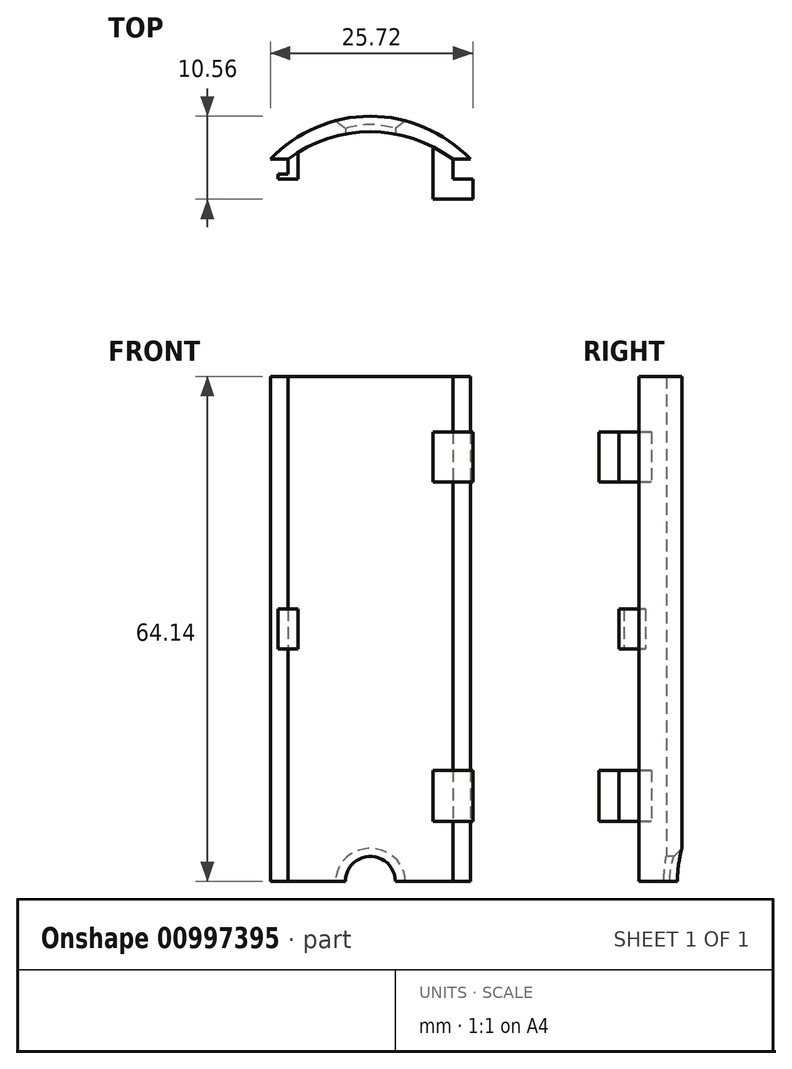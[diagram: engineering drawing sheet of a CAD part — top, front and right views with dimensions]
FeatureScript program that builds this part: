
annotation { "Feature Type Name" : "Feature", "Feature Type Description" : "" }
export const myFeature = defineFeature(function(context is Context, id is Id, definition is map)
    precondition{}
    {
        {
            var Q0;
            Q0=qCreatedBy(makeId("Top.planeOp"),FACE);
            var sketch = newSketch(context, id + "F0", { "sketchPlane" : qUnion([Q0])});
            skArc(sketch, "E0", {"start": v(-9.49, 0) * mm, "mid": v(-22.19, 5.48) * mm, "end": v(-34.89, 0) * mm});
            skPoint(sketch, "E1", {"position": v(-32.67, 0) * mm});
            skPoint(sketch, "E2", {"position": v(-11.7, 0) * mm});
            skArc(sketch, "E3", {"start": v(-11.7, 0) * mm, "mid": v(-22.19, 3.5) * mm, "end": v(-32.67, 0) * mm});
            skLineSegment(sketch, "E4", {"start": v(-34.89, 0) * mm, "end": v(-32.67, 0) * mm});
            skLineSegment(sketch, "E5", {"start": v(-11.7, 0) * mm, "end": v(-9.49, 0) * mm});
            skSolve(sketch);
        }
        {
            var Q0;
            Q0 = qSketchRegion(id + "F0", true);
            extrude(context, id + "F1", {"entities" : qUnion([Q0]), "depth" : 64.13 * mm, "offsetDistance" : 25.4 * mm});
        }
        {
            var Q0;
            Q0=qCreatedBy(makeId("Front.planeOp"),FACE);
            var sketch = newSketch(context, id + "F2", { "sketchPlane" : qUnion([Q0])});
            skLineSegment(sketch, "E6.0", {"start": v(-9.49, 0) * mm, "end": v(-34.89, 0) * mm});
            skCircle(sketch, "E7", {"center": v(-22.19, 0) * mm, "radius": 3.18 * mm});
            skSolve(sketch);
        }
        {
            var Q0;
            Q0 = qSketchRegion(id + "F2", true);
            extrude(context, id + "F3", {"entities" : qUnion([Q0]), "operationType" : NewBodyOperationType.REMOVE, "oppositeDirection" : true, "depth" : 25.4 * mm, "offsetDistance" : 25.4 * mm});
        }
        {
            var Q0;
            Q0=makeQuery(id+"F3.boolean.opBoolean","INTERSECT",EDGE,{"derivedFrom":[makeQuery(id+"F1.opExtrude","SWEPT_FACE",FACE,{"disambiguationData":[OSD([sQuery(id+"F0.wireOp",EDGE,"E0")])]}),makeQuery(id+"F3.opExtrude","SWEPT_FACE",FACE,{"disambiguationData":[OSD([sQuery(id+"F2.wireOp",EDGE,"E7")])]})]});
            chamfer(context, id + "F4", {"entities" : qUnion([Q0]), "width" : 1 * mm, "tangentPropagation" : true});
        }
        {
            var Q0;
            Q0=makeQuery(id+"F1.opExtrude","SWEPT_FACE",FACE,{"disambiguationData":[OSD([sQuery(id+"F0.wireOp",EDGE,"E4")])]});
            var sketch = newSketch(context, id + "F5", { "sketchPlane" : qUnion([Q0])});
            skLineSegment(sketch, "E8.0", {"start": v(-11.7, 64.13) * mm, "end": v(-11.7, 0) * mm});
            skLineSegment(sketch, "E9.bottom", {"start": v(-11.7, 57.09) * mm, "end": v(-14.25, 57.09) * mm});
            skLineSegment(sketch, "E9.top", {"start": v(-11.7, 50.74) * mm, "end": v(-14.25, 50.74) * mm});
            skLineSegment(sketch, "E9.left", {"start": v(-11.7, 57.09) * mm, "end": v(-11.7, 50.74) * mm});
            skLineSegment(sketch, "E9.right", {"start": v(-14.25, 57.09) * mm, "end": v(-14.25, 50.74) * mm});
            skLineSegment(sketch, "E10.bottom", {"start": v(-11.7, 14.1) * mm, "end": v(-14.25, 14.1) * mm});
            skLineSegment(sketch, "E10.top", {"start": v(-11.7, 7.63) * mm, "end": v(-14.25, 7.63) * mm});
            skLineSegment(sketch, "E10.left", {"start": v(-11.7, 14.1) * mm, "end": v(-11.7, 7.63) * mm});
            skLineSegment(sketch, "E10.right", {"start": v(-14.25, 14.1) * mm, "end": v(-14.25, 7.63) * mm});
            skSolve(sketch);
        }
        {
            var Q0;
            {var subQ0=sQuery(id+"F5.wireOp",EDGE,"E10.bottom");var subQ4=sQuery(id+"F5.wireOp",EDGE,"E9.bottom");Q0=qUnion([makeQuery(id+"F5.imprint","IMPRINT",FACE,{"disambiguationData":[TD([[makeQuery(id+"F5.imprint","IMPRINT",EDGE,{"derivedFrom":subQ4}),1.0]])]}),makeQuery(id+"F5.imprint","IMPRINT",FACE,{"disambiguationData":[TD([[makeQuery(id+"F5.imprint","IMPRINT",EDGE,{"derivedFrom":subQ0}),1.0]])]})]);}
            extrude(context, id + "F6", {"entities" : qUnion([Q0]), "operationType" : NewBodyOperationType.ADD, "oppositeDirection" : true, "depth" : 1.78 * mm, "offsetDistance" : 25.4 * mm});
        }
        {
            var Q0;
            {var subQ0=sQuery(id+"F5.wireOp",EDGE,"E10.bottom");var subQ4=sQuery(id+"F5.wireOp",EDGE,"E9.bottom");Q0=qUnion([makeQuery(id+"F5.imprint","IMPRINT",FACE,{"disambiguationData":[TD([[makeQuery(id+"F5.imprint","IMPRINT",EDGE,{"derivedFrom":subQ4}),1.0]])]}),makeQuery(id+"F5.imprint","IMPRINT",FACE,{"disambiguationData":[TD([[makeQuery(id+"F5.imprint","IMPRINT",EDGE,{"derivedFrom":subQ0}),1.0]])]})]);}
            extrude(context, id + "F7", {"entities" : qUnion([Q0]), "operationType" : NewBodyOperationType.ADD, "depth" : 5.08 * mm, "offsetDistance" : 25.4 * mm});
        }
        {
            var Q0;
            {var subQ0=sQuery(id+"F5.wireOp",EDGE,"E8.0");Q0=makeQuery(id+"F7.opExtrude","SWEPT_FACE",FACE,{"disambiguationData":[OSD([subQ0]),TDD([makeQuery(id+"F5.imprint","IMPRINT",EDGE,{"disambiguationData":[TD([[makeQuery(id+"F5.imprint","INTERSECT",VERTEX,{"derivedFrom":[subQ0,sQuery(id+"F5.wireOp",EDGE,"E9.top")]}),1.0]])],"derivedFrom":subQ0})])]});}
            var sketch = newSketch(context, id + "F8", { "sketchPlane" : qUnion([Q0])});
            skLineSegment(sketch, "E11.bottom", {"start": v(-5.08, 57.09) * mm, "end": v(-2.54, 57.09) * mm});
            skLineSegment(sketch, "E11.top", {"start": v(-5.08, 50.74) * mm, "end": v(-2.54, 50.74) * mm});
            skLineSegment(sketch, "E11.left", {"start": v(-5.08, 57.09) * mm, "end": v(-5.08, 50.74) * mm});
            skLineSegment(sketch, "E11.right", {"start": v(-2.54, 57.09) * mm, "end": v(-2.54, 50.74) * mm});
            skLineSegment(sketch, "E12.0.0", {"start": v(0, 7.63) * mm, "end": v(0, 14.1) * mm});
            skLineSegment(sketch, "E12.0.1", {"start": v(-2.54, 14.1) * mm, "end": v(-5.08, 14.1) * mm});
            skLineSegment(sketch, "E12.0.2", {"start": v(-5.08, 14.1) * mm, "end": v(-5.08, 7.63) * mm});
            skLineSegment(sketch, "E12.0.3", {"start": v(-5.08, 7.63) * mm, "end": v(-2.54, 7.63) * mm});
            skLineSegment(sketch, "E13.bottom", {"start": v(-5.08, 14.1) * mm, "end": v(-2.54, 14.1) * mm});
            skLineSegment(sketch, "E13.right", {"start": v(-2.54, 14.1) * mm, "end": v(-2.54, 7.63) * mm});
            skSolve(sketch);
        }
        {
            var Q0;
            Q0 = qSketchRegion(id + "F8", true);
            extrude(context, id + "F9", {"entities" : qUnion([Q0]), "operationType" : NewBodyOperationType.ADD, "depth" : 2.54 * mm, "offsetDistance" : 25.4 * mm});
        }
        {
            var Q0;
            Q0=makeQuery(id+"F1.opExtrude","SWEPT_FACE",FACE,{"disambiguationData":[OSD([sQuery(id+"F0.wireOp",EDGE,"E4")])]});
            var sketch = newSketch(context, id + "F10", { "sketchPlane" : qUnion([Q0])});
            skLineSegment(sketch, "E14.bottom", {"start": v(-32.67, 29.53) * mm, "end": v(-31.4, 29.53) * mm});
            skLineSegment(sketch, "E14.top", {"start": v(-32.67, 34.6) * mm, "end": v(-31.4, 34.6) * mm});
            skLineSegment(sketch, "E14.left", {"start": v(-32.67, 29.53) * mm, "end": v(-32.67, 34.6) * mm});
            skLineSegment(sketch, "E14.right", {"start": v(-31.4, 29.53) * mm, "end": v(-31.4, 34.6) * mm});
            skSolve(sketch);
        }
        {
            var Q0;
            Q0 = qSketchRegion(id + "F10", true);
            extrude(context, id + "F11", {"entities" : qUnion([Q0]), "operationType" : NewBodyOperationType.ADD, "oppositeDirection" : true, "depth" : 1.96 * mm, "offsetDistance" : 25.4 * mm});
        }
        {
            var Q0;
            Q0 = qSketchRegion(id + "F10", true);
            extrude(context, id + "F12", {"entities" : qUnion([Q0]), "operationType" : NewBodyOperationType.ADD, "depth" : 2.54 * mm, "offsetDistance" : 25.4 * mm});
        }
        {
            var Q0;
            Q0=makeQuery(id+"F12.opExtrude","SWEPT_FACE",FACE,{"disambiguationData":[OSD([sQuery(id+"F10.wireOp",EDGE,"E14.left")])]});
            var sketch = newSketch(context, id + "F13", { "sketchPlane" : qUnion([Q0])});
            skLineSegment(sketch, "E15.bottom", {"start": v(2.54, 34.6) * mm, "end": v(1.9, 34.6) * mm});
            skLineSegment(sketch, "E15.top", {"start": v(2.54, 29.53) * mm, "end": v(1.9, 29.53) * mm});
            skLineSegment(sketch, "E15.left", {"start": v(2.54, 34.6) * mm, "end": v(2.54, 29.53) * mm});
            skLineSegment(sketch, "E15.right", {"start": v(1.9, 34.6) * mm, "end": v(1.9, 29.53) * mm});
            skSolve(sketch);
        }
        {
            var Q0;
            Q0 = qSketchRegion(id + "F13", true);
            extrude(context, id + "F14", {"entities" : qUnion([Q0]), "operationType" : NewBodyOperationType.ADD, "depth" : 1.27 * mm, "offsetDistance" : 25.4 * mm});
        }
    });
